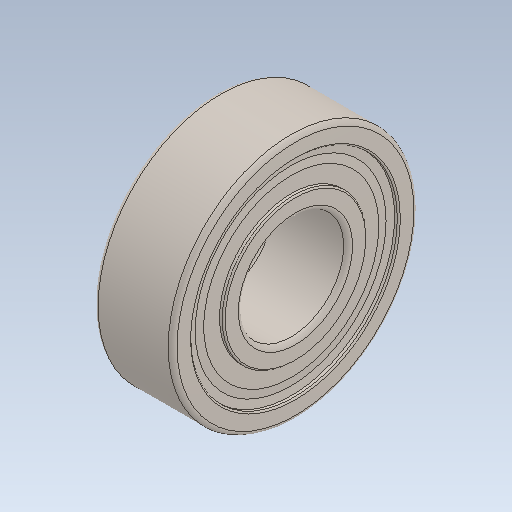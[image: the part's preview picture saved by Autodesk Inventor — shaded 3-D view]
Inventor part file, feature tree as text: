
AUTODESK INVENTOR PART (.ipt)
format: ipt  version: 2020 (Build 240168000, 168)  size: 247,296 bytes
history: native  units: in
note: dims shown in document units (in); Inventor stores cm internally (conversion verified against a paired STEP export)
features: revolve x1
ambient origin geometry x8: Origin, YZ Plane, XZ Plane, XY Plane, X Axis, Y Axis, Z Axis, Center Point
bodies: Solid1 (feature_tree)
feature tree (1):
  revolve  "Revolve1"  [1 undecoded]
note: 1 required parameter value undecoded (feature->parameter linkage not recoverable at this tier; creation-order binding heuristic only, values carry confidence <= 0.55)
